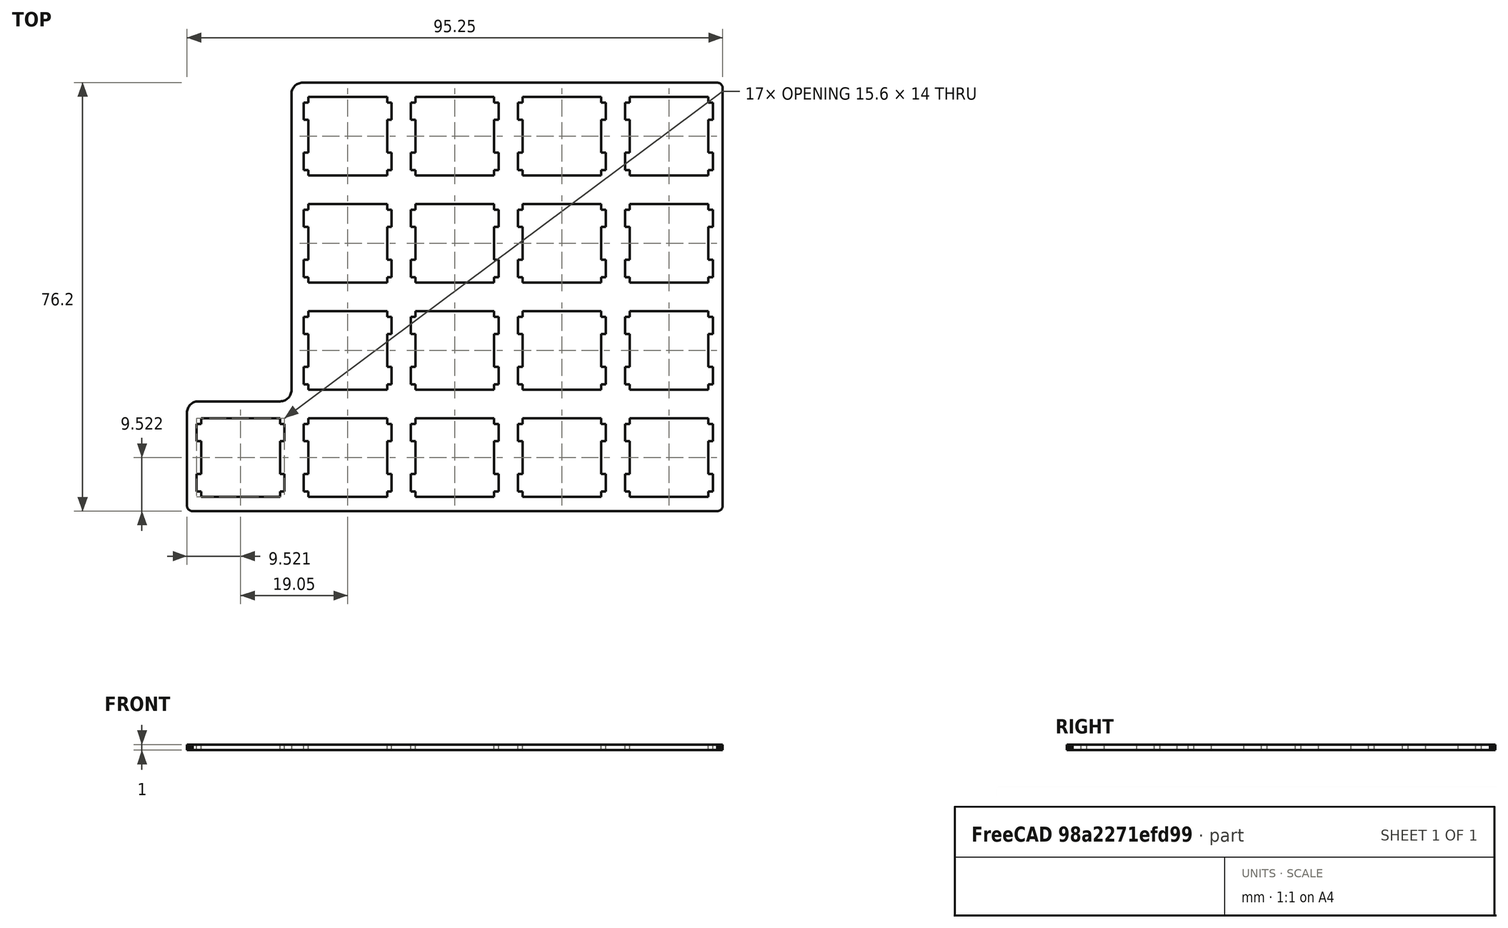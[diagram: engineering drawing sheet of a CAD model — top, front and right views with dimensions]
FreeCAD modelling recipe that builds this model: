
FCSTD DOCUMENT  (FreeCAD 0.20R)
Label: dpad-plate
License: All rights reserved
LicenseURL: http://en.wikipedia.org/wiki/All_rights_reserved
objects: Sketcher::SketchObject×2, PartDesign::Pad×1, PartDesign::Pocket×1, PartDesign::Fillet×1, PartDesign::Body×1
note: 9 computed .brp shape members not serialized (recipe doc carries the construction recipe); baked Part::Feature solids carry a one-line shape summary decoded from their .brp

FEATURE [Sketcher::SketchObject] Sketch
  FullyConstrained = false
  Placement = pos=(0,0,0) rot=(0,0,1;3.14159rad)
  sketch-geometry (424):
    g0: LineSegment StartX=-94.3462 StartY=-76.4575 StartZ=0 EndX=-94.4245 EndY=-76.4551 EndZ=0
    g1: LineSegment StartX=-94.4245 StartY=-76.4551 StartZ=0 EndX=-94.5032 EndY=-76.4452 EndZ=0
    g2: LineSegment StartX=-94.5032 StartY=-76.4452 StartZ=0 EndX=-94.579 EndY=-76.43 EndZ=0
    g3: LineSegment StartX=-94.579 StartY=-76.43 StartZ=0 EndX=-94.6559 EndY=-76.4095 EndZ=0
    g4: LineSegment StartX=-94.6559 StartY=-76.4095 StartZ=0 EndX=-94.729 EndY=-76.382 EndZ=0
    g5: LineSegment StartX=-94.729 StartY=-76.382 StartZ=0 EndX=-94.7995 EndY=-76.3489 EndZ=0
    g6: LineSegment StartX=-94.7995 StartY=-76.3489 StartZ=0 EndX=-94.8683 EndY=-76.3104 EndZ=0
    g7: LineSegment StartX=-94.8683 StartY=-76.3104 StartZ=0 EndX=-94.9332 EndY=-76.2674 EndZ=0
    g8: LineSegment StartX=-94.9332 StartY=-76.2674 StartZ=0 EndX=-94.9949 EndY=-76.218 EndZ=0
    g9: LineSegment StartX=-94.9949 StartY=-76.218 StartZ=0 EndX=-95.0528 EndY=-76.1654 EndZ=0
    g10: LineSegment StartX=-95.0528 StartY=-76.1654 StartZ=0 EndX=-95.1068 EndY=-76.1076 EndZ=0
    g11: LineSegment StartX=-95.1068 StartY=-76.1076 StartZ=0 EndX=-95.1548 EndY=-76.0458 EndZ=0
    g12: LineSegment StartX=-95.1548 StartY=-76.0458 StartZ=0 EndX=-95.1989 EndY=-75.9809 EndZ=0
    g13: LineSegment StartX=-95.1989 StartY=-75.9809 StartZ=0 EndX=-95.2377 EndY=-75.9107 EndZ=0
    g14: LineSegment StartX=-95.2377 StartY=-75.9107 StartZ=0 EndX=-95.2694 EndY=-75.8402 EndZ=0
    g15: LineSegment StartX=-95.2694 StartY=-75.8402 StartZ=0 EndX=-95.2969 EndY=-75.7671 EndZ=0
    g16: LineSegment StartX=-95.2969 StartY=-75.7671 StartZ=0 EndX=-95.3188 EndY=-75.6916 EndZ=0
    g17: LineSegment StartX=-95.3188 StartY=-75.6916 StartZ=0 EndX=-95.334 EndY=-75.6144 EndZ=0
    g18: LineSegment StartX=-95.334 StartY=-75.6144 StartZ=0 EndX=-95.3424 EndY=-75.5357 EndZ=0
    g19: LineSegment StartX=-95.3424 StartY=-75.5357 StartZ=0 EndX=-95.3463 EndY=-75.4574 EndZ=0
    g20: LineSegment StartX=-95.3463 StartY=-75.4574 StartZ=0 EndX=-95.3452 EndY=-1.25677 EndZ=0
    g21: LineSegment StartX=-95.3452 StartY=-1.25677 StartZ=0 EndX=-95.3424 EndY=-1.17822 EndZ=0
    g22: LineSegment StartX=-95.3424 StartY=-1.17822 StartZ=0 EndX=-95.334 EndY=-1.09968 EndZ=0
    g23: LineSegment StartX=-95.334 StartY=-1.09968 StartZ=0 EndX=-95.3188 EndY=-1.02388 EndZ=0
    g24: LineSegment StartX=-95.3188 StartY=-1.02388 StartZ=0 EndX=-95.2969 EndY=-0.946711 EndZ=0
    g25: LineSegment StartX=-95.2969 StartY=-0.946711 StartZ=0 EndX=-95.2694 EndY=-0.873675 EndZ=0
    g26: LineSegment StartX=-95.2694 StartY=-0.873675 StartZ=0 EndX=-95.2377 EndY=-0.803395 EndZ=0
    g27: LineSegment StartX=-95.2377 StartY=-0.803395 StartZ=0 EndX=-95.1989 EndY=-0.734494 EndZ=0
    g28: LineSegment StartX=-95.1989 StartY=-0.734494 StartZ=0 EndX=-95.1548 EndY=-0.669727 EndZ=0
    g29: LineSegment StartX=-95.1548 StartY=-0.669727 StartZ=0 EndX=-95.1068 EndY=-0.607716 EndZ=0
    g30: LineSegment StartX=-95.1068 StartY=-0.607716 StartZ=0 EndX=-95.0528 EndY=-0.549836 EndZ=0
    g31: LineSegment StartX=-95.0528 StartY=-0.549836 StartZ=0 EndX=-94.9949 EndY=-0.496094 EndZ=0
    g32: LineSegment StartX=-94.9949 StartY=-0.496094 StartZ=0 EndX=-94.9332 EndY=-0.447862 EndZ=0
    g33: LineSegment StartX=-94.9332 StartY=-0.447862 StartZ=0 EndX=-94.8683 EndY=-0.403765 EndZ=0
    g34: LineSegment StartX=-94.8683 StartY=-0.403765 StartZ=0 EndX=-94.7995 EndY=-0.365181 EndZ=0
    g35: LineSegment StartX=-94.7995 StartY=-0.365181 StartZ=0 EndX=-94.729 EndY=-0.333485 EndZ=0
    g36: LineSegment StartX=-94.729 StartY=-0.333485 StartZ=0 EndX=-94.6559 EndY=-0.305925 EndZ=0
    g37: LineSegment StartX=-94.6559 StartY=-0.305925 StartZ=0 EndX=-94.579 EndY=-0.283876 EndZ=0
    g38: LineSegment StartX=-94.579 StartY=-0.283876 StartZ=0 EndX=-94.5032 EndY=-0.268718 EndZ=0
    g39: LineSegment StartX=-94.5032 StartY=-0.268718 StartZ=0 EndX=-94.4245 EndY=-0.260449 EndZ=0
    g40: LineSegment StartX=-94.4245 StartY=-0.260449 StartZ=0 EndX=-94.3462 EndY=-0.256315 EndZ=0
    g41: LineSegment StartX=-94.3462 StartY=-0.256315 StartZ=0 EndX=-1.09554 EndY=-0.256315 EndZ=0
    g42: LineSegment StartX=-1.09554 StartY=-0.256315 StartZ=0 EndX=-1.01699 EndY=-0.260449 EndZ=0
    g43: LineSegment StartX=-1.01699 StartY=-0.260449 StartZ=0 EndX=-0.938445 EndY=-0.268718 EndZ=0
    g44: LineSegment StartX=-0.938445 StartY=-0.268718 StartZ=0 EndX=-0.861275 EndY=-0.283876 EndZ=0
    g45: LineSegment StartX=-0.861275 StartY=-0.283876 StartZ=0 EndX=-0.785481 EndY=-0.305925 EndZ=0
    g46: LineSegment StartX=-0.785481 StartY=-0.305925 StartZ=0 EndX=-0.712445 EndY=-0.333485 EndZ=0
    g47: LineSegment StartX=-0.712445 StartY=-0.333485 StartZ=0 EndX=-0.642165 EndY=-0.365181 EndZ=0
    g48: LineSegment StartX=-0.642165 StartY=-0.365181 StartZ=0 EndX=-0.571885 EndY=-0.403765 EndZ=0
    g49: LineSegment StartX=-0.571885 StartY=-0.403765 StartZ=0 EndX=-0.507118 EndY=-0.447862 EndZ=0
    g50: LineSegment StartX=-0.507118 StartY=-0.447862 StartZ=0 EndX=-0.445107 EndY=-0.496094 EndZ=0
    g51: LineSegment StartX=-0.445107 StartY=-0.496094 StartZ=0 EndX=-0.38723 EndY=-0.549836 EndZ=0
    g52: LineSegment StartX=-0.38723 StartY=-0.549836 StartZ=0 EndX=-0.334863 EndY=-0.607716 EndZ=0
    g53: LineSegment StartX=-0.334863 StartY=-0.607716 StartZ=0 EndX=-0.285254 EndY=-0.669727 EndZ=0
    g54: LineSegment StartX=-0.285254 StartY=-0.669727 StartZ=0 EndX=-0.242535 EndY=-0.734494 EndZ=0
    g55: LineSegment StartX=-0.242535 StartY=-0.734494 StartZ=0 EndX=-0.20395 EndY=-0.803395 EndZ=0
    g56: LineSegment StartX=-0.20395 StartY=-0.803395 StartZ=0 EndX=-0.170877 EndY=-0.873675 EndZ=0
    g57: LineSegment StartX=-0.170877 StartY=-0.873675 StartZ=0 EndX=-0.143316 EndY=-0.946711 EndZ=0
    g58: LineSegment StartX=-0.143316 StartY=-0.946711 StartZ=0 EndX=-0.122645 EndY=-1.02388 EndZ=0
    g59: LineSegment StartX=-0.122645 StartY=-1.02388 StartZ=0 EndX=-0.107487 EndY=-1.09968 EndZ=0
    g60: LineSegment StartX=-0.107487 StartY=-1.09968 StartZ=0 EndX=-0.0978408 EndY=-1.17822 EndZ=0
    g61: LineSegment StartX=-0.0978408 StartY=-1.17822 StartZ=0 EndX=-0.0950846 EndY=-1.25677 EndZ=0
    g62: LineSegment StartX=-0.0950846 StartY=-1.25677 StartZ=0 EndX=-0.0950846 EndY=-75.4574 EndZ=0
    g63: LineSegment StartX=-0.0950846 StartY=-75.4574 StartZ=0 EndX=-0.0978408 EndY=-75.5357 EndZ=0
    g64: LineSegment StartX=-0.0978408 StartY=-75.5357 StartZ=0 EndX=-0.107487 EndY=-75.6144 EndZ=0
    g65: LineSegment StartX=-0.107487 StartY=-75.6144 StartZ=0 EndX=-0.122645 EndY=-75.6916 EndZ=0
    g66: LineSegment StartX=-0.122645 StartY=-75.6916 StartZ=0 EndX=-0.143316 EndY=-75.7671 EndZ=0
    g67: LineSegment StartX=-0.143316 StartY=-75.7671 StartZ=0 EndX=-0.170877 EndY=-75.8402 EndZ=0
    g68: LineSegment StartX=-0.170877 StartY=-75.8402 StartZ=0 EndX=-0.20395 EndY=-75.9107 EndZ=0
    g69: LineSegment StartX=-0.20395 StartY=-75.9107 StartZ=0 EndX=-0.242535 EndY=-75.9809 EndZ=0
    g70: LineSegment StartX=-0.242535 StartY=-75.9809 StartZ=0 EndX=-0.285254 EndY=-76.0458 EndZ=0
    g71: LineSegment StartX=-0.285254 StartY=-76.0458 StartZ=0 EndX=-0.334863 EndY=-76.1076 EndZ=0
    g72: LineSegment StartX=-0.334863 StartY=-76.1076 StartZ=0 EndX=-0.38723 EndY=-76.1654 EndZ=0
    g73: LineSegment StartX=-0.38723 StartY=-76.1654 StartZ=0 EndX=-0.445107 EndY=-76.218 EndZ=0
    g74: LineSegment StartX=-0.445107 StartY=-76.218 StartZ=0 EndX=-0.507118 EndY=-76.2674 EndZ=0
    g75: LineSegment StartX=-0.507118 StartY=-76.2674 StartZ=0 EndX=-0.571885 EndY=-76.3104 EndZ=0
    g76: LineSegment StartX=-0.571885 StartY=-76.3104 StartZ=0 EndX=-0.642165 EndY=-76.3489 EndZ=0
    g77: LineSegment StartX=-0.642165 StartY=-76.3489 StartZ=0 EndX=-0.712445 EndY=-76.382 EndZ=0
    g78: LineSegment StartX=-0.712445 StartY=-76.382 StartZ=0 EndX=-0.785481 EndY=-76.4095 EndZ=0
    g79: LineSegment StartX=-0.785481 StartY=-76.4095 StartZ=0 EndX=-0.861275 EndY=-76.43 EndZ=0
    g80: LineSegment StartX=-0.861275 StartY=-76.43 StartZ=0 EndX=-0.938445 EndY=-76.4452 EndZ=0
    g81: LineSegment StartX=-0.938445 StartY=-76.4452 StartZ=0 EndX=-1.01699 EndY=-76.4551 EndZ=0
    g82: LineSegment StartX=-1.01699 StartY=-76.4551 StartZ=0 EndX=-1.09554 EndY=-76.4575 EndZ=0
    g83: LineSegment StartX=-1.09554 StartY=-76.4575 StartZ=0 EndX=-94.3462 EndY=-76.4575 EndZ=0
    g84: LineSegment StartX=-2.62103 StartY=-16.7817 StartZ=0 EndX=-2.62103 EndY=-15.7827 EndZ=0
    g85: LineSegment StartX=-2.62103 StartY=-15.7827 StartZ=0 EndX=-1.82039 EndY=-15.7827 EndZ=0
    g86: LineSegment StartX=-1.82039 StartY=-15.7827 StartZ=0 EndX=-1.82039 EndY=-12.6835 EndZ=0
    g87: LineSegment StartX=-1.82039 StartY=-12.6835 StartZ=0 EndX=-2.62103 EndY=-12.6835 EndZ=0
    g88: LineSegment StartX=-2.62103 StartY=-12.6835 StartZ=0 EndX=-2.62103 EndY=-6.88192 EndZ=0
    g89: LineSegment StartX=-2.62103 StartY=-6.88192 StartZ=0 EndX=-1.82039 EndY=-6.88192 EndZ=0
    g90: LineSegment StartX=-1.82039 StartY=-6.88192 StartZ=0 EndX=-1.82039 EndY=-3.78273 EndZ=0
    g91: LineSegment StartX=-1.82039 StartY=-3.78273 StartZ=0 EndX=-2.62103 EndY=-3.78273 EndZ=0
    g92: LineSegment StartX=-2.62103 StartY=-3.78273 StartZ=0 EndX=-2.62103 EndY=-2.78226 EndZ=0
    g93: LineSegment StartX=-2.62103 StartY=-2.78226 StartZ=0 EndX=-16.6205 EndY=-2.78226 EndZ=0
    g94: LineSegment StartX=-16.6205 StartY=-2.78226 StartZ=0 EndX=-16.6205 EndY=-3.78273 EndZ=0
    g95: LineSegment StartX=-16.6205 StartY=-3.78273 StartZ=0 EndX=-17.4212 EndY=-3.78273 EndZ=0
    g96: LineSegment StartX=-17.4212 StartY=-3.78273 StartZ=0 EndX=-17.4212 EndY=-6.88192 EndZ=0
    g97: LineSegment StartX=-17.4212 StartY=-6.88192 StartZ=0 EndX=-16.6205 EndY=-6.88192 EndZ=0
    g98: LineSegment StartX=-16.6205 StartY=-6.88192 StartZ=0 EndX=-16.6205 EndY=-12.6835 EndZ=0
    g99: LineSegment StartX=-16.6205 StartY=-12.6835 StartZ=0 EndX=-17.4212 EndY=-12.6835 EndZ=0
    g100: LineSegment StartX=-17.4212 StartY=-12.6835 StartZ=0 EndX=-17.4212 EndY=-15.7827 EndZ=0
    g101: LineSegment StartX=-17.4212 StartY=-15.7827 StartZ=0 EndX=-16.6205 EndY=-15.7827 EndZ=0
    g102: LineSegment StartX=-16.6205 StartY=-15.7827 StartZ=0 EndX=-16.6205 EndY=-16.7817 EndZ=0
    g103: LineSegment StartX=-16.6205 StartY=-16.7817 StartZ=0 EndX=-2.62103 EndY=-16.7817 EndZ=0
    g104: LineSegment StartX=-21.671 StartY=-16.7817 StartZ=0 EndX=-21.671 EndY=-15.7827 EndZ=0
    g105: LineSegment StartX=-21.671 StartY=-15.7827 StartZ=0 EndX=-20.8704 EndY=-15.7827 EndZ=0
    g106: LineSegment StartX=-20.8704 StartY=-15.7827 StartZ=0 EndX=-20.8704 EndY=-12.6835 EndZ=0
    g107: LineSegment StartX=-20.8704 StartY=-12.6835 StartZ=0 EndX=-21.671 EndY=-12.6835 EndZ=0
    g108: LineSegment StartX=-21.671 StartY=-12.6835 StartZ=0 EndX=-21.671 EndY=-6.88192 EndZ=0
    g109: LineSegment StartX=-21.671 StartY=-6.88192 StartZ=0 EndX=-20.8704 EndY=-6.88192 EndZ=0
    g110: LineSegment StartX=-20.8704 StartY=-6.88192 StartZ=0 EndX=-20.8704 EndY=-3.78273 EndZ=0
    g111: LineSegment StartX=-20.8704 StartY=-3.78273 StartZ=0 EndX=-21.671 EndY=-3.78273 EndZ=0
    g112: LineSegment StartX=-21.671 StartY=-3.78273 StartZ=0 EndX=-21.671 EndY=-2.78226 EndZ=0
    g113: LineSegment StartX=-21.671 StartY=-2.78226 StartZ=0 EndX=-35.6704 EndY=-2.78226 EndZ=0
    g114: LineSegment StartX=-35.6704 StartY=-2.78226 StartZ=0 EndX=-35.6704 EndY=-3.78273 EndZ=0
    g115: LineSegment StartX=-35.6704 StartY=-3.78273 StartZ=0 EndX=-36.4712 EndY=-3.78273 EndZ=0
    g116: LineSegment StartX=-36.4712 StartY=-3.78273 StartZ=0 EndX=-36.4712 EndY=-6.88192 EndZ=0
    g117: LineSegment StartX=-36.4712 StartY=-6.88192 StartZ=0 EndX=-35.6704 EndY=-6.88192 EndZ=0
    g118: LineSegment StartX=-35.6704 StartY=-6.88192 StartZ=0 EndX=-35.6704 EndY=-12.6835 EndZ=0
    g119: LineSegment StartX=-35.6704 StartY=-12.6835 StartZ=0 EndX=-36.4712 EndY=-12.6835 EndZ=0
    g120: LineSegment StartX=-36.4712 StartY=-12.6835 StartZ=0 EndX=-36.4712 EndY=-15.7827 EndZ=0
    g121: LineSegment StartX=-36.4712 StartY=-15.7827 StartZ=0 EndX=-35.6704 EndY=-15.7827 EndZ=0
    g122: LineSegment StartX=-35.6704 StartY=-15.7827 StartZ=0 EndX=-35.6704 EndY=-16.7817 EndZ=0
    g123: LineSegment StartX=-35.6704 StartY=-16.7817 StartZ=0 EndX=-21.671 EndY=-16.7817 EndZ=0
    g124: LineSegment StartX=-40.7211 StartY=-16.7817 StartZ=0 EndX=-40.7211 EndY=-15.7827 EndZ=0
    g125: LineSegment StartX=-40.7211 StartY=-15.7827 StartZ=0 EndX=-39.9203 EndY=-15.7827 EndZ=0
    g126: LineSegment StartX=-39.9203 StartY=-15.7827 StartZ=0 EndX=-39.9203 EndY=-12.6835 EndZ=0
    g127: LineSegment StartX=-39.9203 StartY=-12.6835 StartZ=0 EndX=-40.7211 EndY=-12.6835 EndZ=0
    g128: LineSegment StartX=-40.7211 StartY=-12.6835 StartZ=0 EndX=-40.7211 EndY=-6.88192 EndZ=0
    g129: LineSegment StartX=-40.7211 StartY=-6.88192 StartZ=0 EndX=-39.9203 EndY=-6.88192 EndZ=0
    g130: LineSegment StartX=-39.9203 StartY=-6.88192 StartZ=0 EndX=-39.9203 EndY=-3.78273 EndZ=0
    g131: LineSegment StartX=-39.9203 StartY=-3.78273 StartZ=0 EndX=-40.7211 EndY=-3.78273 EndZ=0
    g132: LineSegment StartX=-40.7211 StartY=-3.78273 StartZ=0 EndX=-40.7211 EndY=-2.78226 EndZ=0
    g133: LineSegment StartX=-40.7211 StartY=-2.78226 StartZ=0 EndX=-54.7204 EndY=-2.78226 EndZ=0
    g134: LineSegment StartX=-54.7204 StartY=-2.78226 StartZ=0 EndX=-54.7204 EndY=-3.78273 EndZ=0
    g135: LineSegment StartX=-54.7204 StartY=-3.78273 StartZ=0 EndX=-55.5212 EndY=-3.78273 EndZ=0
    g136: LineSegment StartX=-55.5212 StartY=-3.78273 StartZ=0 EndX=-55.5212 EndY=-6.88192 EndZ=0
    g137: LineSegment StartX=-55.5212 StartY=-6.88192 StartZ=0 EndX=-54.7204 EndY=-6.88192 EndZ=0
    g138: LineSegment StartX=-54.7204 StartY=-6.88192 StartZ=0 EndX=-54.7204 EndY=-12.6835 EndZ=0
    g139: LineSegment StartX=-54.7204 StartY=-12.6835 StartZ=0 EndX=-55.5212 EndY=-12.6835 EndZ=0
    g140: LineSegment StartX=-55.5212 StartY=-12.6835 StartZ=0 EndX=-55.5212 EndY=-15.7827 EndZ=0
    g141: LineSegment StartX=-55.5212 StartY=-15.7827 StartZ=0 EndX=-54.7204 EndY=-15.7827 EndZ=0
    g142: LineSegment StartX=-54.7204 StartY=-15.7827 StartZ=0 EndX=-54.7204 EndY=-16.7817 EndZ=0
    g143: LineSegment StartX=-54.7204 StartY=-16.7817 StartZ=0 EndX=-40.7211 EndY=-16.7817 EndZ=0
    g144: LineSegment StartX=-59.7711 StartY=-16.7817 StartZ=0 EndX=-59.7711 EndY=-15.7827 EndZ=0
    g145: LineSegment StartX=-59.7711 StartY=-15.7827 StartZ=0 EndX=-58.9703 EndY=-15.7827 EndZ=0
    g146: LineSegment StartX=-58.9703 StartY=-15.7827 StartZ=0 EndX=-58.9703 EndY=-12.6835 EndZ=0
    g147: LineSegment StartX=-58.9703 StartY=-12.6835 StartZ=0 EndX=-59.7711 EndY=-12.6835 EndZ=0
    g148: LineSegment StartX=-59.7711 StartY=-12.6835 StartZ=0 EndX=-59.7711 EndY=-6.88192 EndZ=0
    g149: LineSegment StartX=-59.7711 StartY=-6.88192 StartZ=0 EndX=-58.9703 EndY=-6.88192 EndZ=0
    g150: LineSegment StartX=-58.9703 StartY=-6.88192 StartZ=0 EndX=-58.9703 EndY=-3.78273 EndZ=0
    g151: LineSegment StartX=-58.9703 StartY=-3.78273 StartZ=0 EndX=-59.7711 EndY=-3.78273 EndZ=0
    g152: LineSegment StartX=-59.7711 StartY=-3.78273 StartZ=0 EndX=-59.7711 EndY=-2.78226 EndZ=0
    g153: LineSegment StartX=-59.7711 StartY=-2.78226 StartZ=0 EndX=-73.7704 EndY=-2.78226 EndZ=0
    g154: LineSegment StartX=-73.7704 StartY=-2.78226 StartZ=0 EndX=-73.7704 EndY=-3.78273 EndZ=0
    g155: LineSegment StartX=-73.7704 StartY=-3.78273 StartZ=0 EndX=-74.5712 EndY=-3.78273 EndZ=0
    g156: LineSegment StartX=-74.5712 StartY=-3.78273 StartZ=0 EndX=-74.5712 EndY=-6.88192 EndZ=0
    g157: LineSegment StartX=-74.5712 StartY=-6.88192 StartZ=0 EndX=-73.7704 EndY=-6.88192 EndZ=0
    g158: LineSegment StartX=-73.7704 StartY=-6.88192 StartZ=0 EndX=-73.7704 EndY=-12.6835 EndZ=0
    g159: LineSegment StartX=-73.7704 StartY=-12.6835 StartZ=0 EndX=-74.5712 EndY=-12.6835 EndZ=0
    g160: LineSegment StartX=-74.5712 StartY=-12.6835 StartZ=0 EndX=-74.5712 EndY=-15.7827 EndZ=0
    g161: LineSegment StartX=-74.5712 StartY=-15.7827 StartZ=0 EndX=-73.7704 EndY=-15.7827 EndZ=0
    g162: LineSegment StartX=-73.7704 StartY=-15.7827 StartZ=0 EndX=-73.7704 EndY=-16.7817 EndZ=0
    g163: LineSegment StartX=-73.7704 StartY=-16.7817 StartZ=0 EndX=-59.7711 EndY=-16.7817 EndZ=0
    g164: LineSegment StartX=-78.8211 StartY=-16.7817 StartZ=0 EndX=-78.8211 EndY=-15.7827 EndZ=0
    g165: LineSegment StartX=-78.8211 StartY=-15.7827 StartZ=0 EndX=-78.0203 EndY=-15.7827 EndZ=0
    g166: LineSegment StartX=-78.0203 StartY=-15.7827 StartZ=0 EndX=-78.0203 EndY=-12.6835 EndZ=0
    g167: LineSegment StartX=-78.0203 StartY=-12.6835 StartZ=0 EndX=-78.8211 EndY=-12.6835 EndZ=0
    g168: LineSegment StartX=-78.8211 StartY=-12.6835 StartZ=0 EndX=-78.8211 EndY=-6.88192 EndZ=0
    g169: LineSegment StartX=-78.8211 StartY=-6.88192 StartZ=0 EndX=-78.0203 EndY=-6.88192 EndZ=0
    g170: LineSegment StartX=-78.0203 StartY=-6.88192 StartZ=0 EndX=-78.0203 EndY=-3.78273 EndZ=0
    g171: LineSegment StartX=-78.0203 StartY=-3.78273 StartZ=0 EndX=-78.8211 EndY=-3.78273 EndZ=0
    g172: LineSegment StartX=-78.8211 StartY=-3.78273 StartZ=0 EndX=-78.8211 EndY=-2.78226 EndZ=0
    g173: LineSegment StartX=-78.8211 StartY=-2.78226 StartZ=0 EndX=-92.8204 EndY=-2.78226 EndZ=0
    g174: LineSegment StartX=-92.8204 StartY=-2.78226 StartZ=0 EndX=-92.8204 EndY=-3.78273 EndZ=0
    g175: LineSegment StartX=-92.8204 StartY=-3.78273 StartZ=0 EndX=-93.6198 EndY=-3.78273 EndZ=0
    g176: LineSegment StartX=-93.6198 StartY=-3.78273 StartZ=0 EndX=-93.6198 EndY=-6.88192 EndZ=0
    g177: LineSegment StartX=-93.6198 StartY=-6.88192 StartZ=0 EndX=-92.8204 EndY=-6.88192 EndZ=0
    g178: LineSegment StartX=-92.8204 StartY=-6.88192 StartZ=0 EndX=-92.8204 EndY=-12.6835 EndZ=0
    g179: LineSegment StartX=-92.8204 StartY=-12.6835 StartZ=0 EndX=-93.6198 EndY=-12.6835 EndZ=0
    g180: LineSegment StartX=-93.6198 StartY=-12.6835 StartZ=0 EndX=-93.6198 EndY=-15.7827 EndZ=0
    g181: LineSegment StartX=-93.6198 StartY=-15.7827 StartZ=0 EndX=-92.8204 EndY=-15.7827 EndZ=0
    g182: LineSegment StartX=-92.8204 StartY=-15.7827 StartZ=0 EndX=-92.8204 EndY=-16.7817 EndZ=0
    g183: LineSegment StartX=-92.8204 StartY=-16.7817 StartZ=0 EndX=-78.8211 EndY=-16.7817 EndZ=0
    g184: LineSegment StartX=-21.671 StartY=-35.8316 StartZ=0 EndX=-21.671 EndY=-34.8327 EndZ=0
    g185: LineSegment StartX=-21.671 StartY=-34.8327 StartZ=0 EndX=-20.8704 EndY=-34.8327 EndZ=0
    g186: LineSegment StartX=-20.8704 StartY=-34.8327 StartZ=0 EndX=-20.8704 EndY=-31.7321 EndZ=0
    g187: LineSegment StartX=-20.8704 StartY=-31.7321 StartZ=0 EndX=-21.671 EndY=-31.7321 EndZ=0
    g188: LineSegment StartX=-21.671 StartY=-31.7321 StartZ=0 EndX=-21.671 EndY=-25.9319 EndZ=0
    g189: LineSegment StartX=-21.671 StartY=-25.9319 StartZ=0 EndX=-20.8704 EndY=-25.9319 EndZ=0
    g190: LineSegment StartX=-20.8704 StartY=-25.9319 StartZ=0 EndX=-20.8704 EndY=-22.8327 EndZ=0
    g191: LineSegment StartX=-20.8704 StartY=-22.8327 StartZ=0 EndX=-21.671 EndY=-22.8327 EndZ=0
    g192: LineSegment StartX=-21.671 StartY=-22.8327 StartZ=0 EndX=-21.671 EndY=-21.8323 EndZ=0
    g193: LineSegment StartX=-21.671 StartY=-21.8323 StartZ=0 EndX=-35.6704 EndY=-21.8323 EndZ=0
    g194: LineSegment StartX=-35.6704 StartY=-21.8323 StartZ=0 EndX=-35.6704 EndY=-22.8327 EndZ=0
    g195: LineSegment StartX=-35.6704 StartY=-22.8327 StartZ=0 EndX=-36.4712 EndY=-22.8327 EndZ=0
    g196: LineSegment StartX=-36.4712 StartY=-22.8327 StartZ=0 EndX=-36.4712 EndY=-25.9319 EndZ=0
    g197: LineSegment StartX=-36.4712 StartY=-25.9319 StartZ=0 EndX=-35.6704 EndY=-25.9319 EndZ=0
    g198: LineSegment StartX=-35.6704 StartY=-25.9319 StartZ=0 EndX=-35.6704 EndY=-31.7321 EndZ=0
    g199: LineSegment StartX=-35.6704 StartY=-31.7321 StartZ=0 EndX=-36.4712 EndY=-31.7321 EndZ=0
    g200: LineSegment StartX=-36.4712 StartY=-31.7321 StartZ=0 EndX=-36.4712 EndY=-34.8327 EndZ=0
    g201: LineSegment StartX=-36.4712 StartY=-34.8327 StartZ=0 EndX=-35.6704 EndY=-34.8327 EndZ=0
    g202: LineSegment StartX=-35.6704 StartY=-34.8327 StartZ=0 EndX=-35.6704 EndY=-35.8316 EndZ=0
    g203: LineSegment StartX=-35.6704 StartY=-35.8316 StartZ=0 EndX=-21.671 EndY=-35.8316 EndZ=0
    g204: LineSegment StartX=-40.7211 StartY=-35.8316 StartZ=0 EndX=-40.7211 EndY=-34.8327 EndZ=0
    g205: LineSegment StartX=-40.7211 StartY=-34.8327 StartZ=0 EndX=-39.9203 EndY=-34.8327 EndZ=0
    g206: LineSegment StartX=-39.9203 StartY=-34.8327 StartZ=0 EndX=-39.9203 EndY=-31.7321 EndZ=0
    g207: LineSegment StartX=-39.9203 StartY=-31.7321 StartZ=0 EndX=-40.7211 EndY=-31.7321 EndZ=0
    g208: LineSegment StartX=-40.7211 StartY=-31.7321 StartZ=0 EndX=-40.7211 EndY=-25.9319 EndZ=0
    g209: LineSegment StartX=-40.7211 StartY=-25.9319 StartZ=0 EndX=-39.9203 EndY=-25.9319 EndZ=0
    g210: LineSegment StartX=-39.9203 StartY=-25.9319 StartZ=0 EndX=-39.9203 EndY=-22.8327 EndZ=0
    g211: LineSegment StartX=-39.9203 StartY=-22.8327 StartZ=0 EndX=-40.7211 EndY=-22.8327 EndZ=0
    g212: LineSegment StartX=-40.7211 StartY=-22.8327 StartZ=0 EndX=-40.7211 EndY=-21.8323 EndZ=0
    g213: LineSegment StartX=-40.7211 StartY=-21.8323 StartZ=0 EndX=-54.7204 EndY=-21.8323 EndZ=0
    g214: LineSegment StartX=-54.7204 StartY=-21.8323 StartZ=0 EndX=-54.7204 EndY=-22.8327 EndZ=0
    g215: LineSegment StartX=-54.7204 StartY=-22.8327 StartZ=0 EndX=-55.5212 EndY=-22.8327 EndZ=0
    g216: LineSegment StartX=-55.5212 StartY=-22.8327 StartZ=0 EndX=-55.5212 EndY=-25.9319 EndZ=0
    g217: LineSegment StartX=-55.5212 StartY=-25.9319 StartZ=0 EndX=-54.7204 EndY=-25.9319 EndZ=0
    g218: LineSegment StartX=-54.7204 StartY=-25.9319 StartZ=0 EndX=-54.7204 EndY=-31.7321 EndZ=0
    g219: LineSegment StartX=-54.7204 StartY=-31.7321 StartZ=0 EndX=-55.5212 EndY=-31.7321 EndZ=0
    g220: LineSegment StartX=-55.5212 StartY=-31.7321 StartZ=0 EndX=-55.5212 EndY=-34.8327 EndZ=0
    g221: LineSegment StartX=-55.5212 StartY=-34.8327 StartZ=0 EndX=-54.7204 EndY=-34.8327 EndZ=0
    g222: LineSegment StartX=-54.7204 StartY=-34.8327 StartZ=0 EndX=-54.7204 EndY=-35.8316 EndZ=0
    g223: LineSegment StartX=-54.7204 StartY=-35.8316 StartZ=0 EndX=-40.7211 EndY=-35.8316 EndZ=0
    g224: LineSegment StartX=-59.7711 StartY=-35.8316 StartZ=0 EndX=-59.7711 EndY=-34.8327 EndZ=0
    g225: LineSegment StartX=-59.7711 StartY=-34.8327 StartZ=0 EndX=-58.9703 EndY=-34.8327 EndZ=0
    g226: LineSegment StartX=-58.9703 StartY=-34.8327 StartZ=0 EndX=-58.9703 EndY=-31.7321 EndZ=0
    g227: LineSegment StartX=-58.9703 StartY=-31.7321 StartZ=0 EndX=-59.7711 EndY=-31.7321 EndZ=0
    g228: LineSegment StartX=-59.7711 StartY=-31.7321 StartZ=0 EndX=-59.7711 EndY=-25.9319 EndZ=0
    g229: LineSegment StartX=-59.7711 StartY=-25.9319 StartZ=0 EndX=-58.9703 EndY=-25.9319 EndZ=0
    g230: LineSegment StartX=-58.9703 StartY=-25.9319 StartZ=0 EndX=-58.9703 EndY=-22.8327 EndZ=0
    g231: LineSegment StartX=-58.9703 StartY=-22.8327 StartZ=0 EndX=-59.7711 EndY=-22.8327 EndZ=0
    g232: LineSegment StartX=-59.7711 StartY=-22.8327 StartZ=0 EndX=-59.7711 EndY=-21.8323 EndZ=0
    g233: LineSegment StartX=-59.7711 StartY=-21.8323 StartZ=0 EndX=-73.7704 EndY=-21.8323 EndZ=0
    g234: LineSegment StartX=-73.7704 StartY=-21.8323 StartZ=0 EndX=-73.7704 EndY=-22.8327 EndZ=0
    g235: LineSegment StartX=-73.7704 StartY=-22.8327 StartZ=0 EndX=-74.5712 EndY=-22.8327 EndZ=0
    g236: LineSegment StartX=-74.5712 StartY=-22.8327 StartZ=0 EndX=-74.5712 EndY=-25.9319 EndZ=0
    g237: LineSegment StartX=-74.5712 StartY=-25.9319 StartZ=0 EndX=-73.7704 EndY=-25.9319 EndZ=0
    g238: LineSegment StartX=-73.7704 StartY=-25.9319 StartZ=0 EndX=-73.7704 EndY=-31.7321 EndZ=0
    g239: LineSegment StartX=-73.7704 StartY=-31.7321 StartZ=0 EndX=-74.5712 EndY=-31.7321 EndZ=0
    g240: LineSegment StartX=-74.5712 StartY=-31.7321 StartZ=0 EndX=-74.5712 EndY=-34.8327 EndZ=0
    g241: LineSegment StartX=-74.5712 StartY=-34.8327 StartZ=0 EndX=-73.7704 EndY=-34.8327 EndZ=0
    g242: LineSegment StartX=-73.7704 StartY=-34.8327 StartZ=0 EndX=-73.7704 EndY=-35.8316 EndZ=0
    g243: LineSegment StartX=-73.7704 StartY=-35.8316 StartZ=0 EndX=-59.7711 EndY=-35.8316 EndZ=0
    g244: LineSegment StartX=-78.8211 StartY=-35.8316 StartZ=0 EndX=-78.8211 EndY=-34.8327 EndZ=0
    g245: LineSegment StartX=-78.8211 StartY=-34.8327 StartZ=0 EndX=-78.0203 EndY=-34.8327 EndZ=0
    g246: LineSegment StartX=-78.0203 StartY=-34.8327 StartZ=0 EndX=-78.0203 EndY=-31.7321 EndZ=0
    g247: LineSegment StartX=-78.0203 StartY=-31.7321 StartZ=0 EndX=-78.8211 EndY=-31.7321 EndZ=0
    g248: LineSegment StartX=-78.8211 StartY=-31.7321 StartZ=0 EndX=-78.8211 EndY=-25.9319 EndZ=0
    g249: LineSegment StartX=-78.8211 StartY=-25.9319 StartZ=0 EndX=-78.0203 EndY=-25.9319 EndZ=0
    g250: LineSegment StartX=-78.0203 StartY=-25.9319 StartZ=0 EndX=-78.0203 EndY=-22.8327 EndZ=0
    g251: LineSegment StartX=-78.0203 StartY=-22.8327 StartZ=0 EndX=-78.8211 EndY=-22.8327 EndZ=0
    g252: LineSegment StartX=-78.8211 StartY=-22.8327 StartZ=0 EndX=-78.8211 EndY=-21.8323 EndZ=0
    g253: LineSegment StartX=-78.8211 StartY=-21.8323 StartZ=0 EndX=-92.8204 EndY=-21.8323 EndZ=0
    g254: LineSegment StartX=-92.8204 StartY=-21.8323 StartZ=0 EndX=-92.8204 EndY=-22.8327 EndZ=0
    g255: LineSegment StartX=-92.8204 StartY=-22.8327 StartZ=0 EndX=-93.6198 EndY=-22.8327 EndZ=0
    g256: LineSegment StartX=-93.6198 StartY=-22.8327 StartZ=0 EndX=-93.6198 EndY=-25.9319 EndZ=0
    g257: LineSegment StartX=-93.6198 StartY=-25.9319 StartZ=0 EndX=-92.8204 EndY=-25.9319 EndZ=0
    g258: LineSegment StartX=-92.8204 StartY=-25.9319 StartZ=0 EndX=-92.8204 EndY=-31.7321 EndZ=0
    g259: LineSegment StartX=-92.8204 StartY=-31.7321 StartZ=0 EndX=-93.6198 EndY=-31.7321 EndZ=0
    g260: LineSegment StartX=-93.6198 StartY=-31.7321 StartZ=0 EndX=-93.6198 EndY=-34.8327 EndZ=0
    g261: LineSegment StartX=-93.6198 StartY=-34.8327 StartZ=0 EndX=-92.8204 EndY=-34.8327 EndZ=0
    g262: LineSegment StartX=-92.8204 StartY=-34.8327 StartZ=0 EndX=-92.8204 EndY=-35.8316 EndZ=0
    g263: LineSegment StartX=-92.8204 StartY=-35.8316 StartZ=0 EndX=-78.8211 EndY=-35.8316 EndZ=0
    g264: LineSegment StartX=-21.671 StartY=-54.8816 StartZ=0 EndX=-21.671 EndY=-53.8826 EndZ=0
    g265: LineSegment StartX=-21.671 StartY=-53.8826 StartZ=0 EndX=-20.8704 EndY=-53.8826 EndZ=0
    g266: LineSegment StartX=-20.8704 StartY=-53.8826 StartZ=0 EndX=-20.8704 EndY=-50.782 EndZ=0
    g267: LineSegment StartX=-20.8704 StartY=-50.782 StartZ=0 EndX=-21.671 EndY=-50.782 EndZ=0
    g268: LineSegment StartX=-21.671 StartY=-50.782 StartZ=0 EndX=-21.671 EndY=-44.982 EndZ=0
    g269: LineSegment StartX=-21.671 StartY=-44.982 StartZ=0 EndX=-20.8704 EndY=-44.982 EndZ=0
    g270: LineSegment StartX=-20.8704 StartY=-44.982 StartZ=0 EndX=-20.8704 EndY=-41.8828 EndZ=0
    g271: LineSegment StartX=-20.8704 StartY=-41.8828 StartZ=0 EndX=-21.671 EndY=-41.8828 EndZ=0
    g272: LineSegment StartX=-21.671 StartY=-41.8828 StartZ=0 EndX=-21.671 EndY=-40.8824 EndZ=0
    g273: LineSegment StartX=-21.671 StartY=-40.8824 StartZ=0 EndX=-35.6704 EndY=-40.8824 EndZ=0
    g274: LineSegment StartX=-35.6704 StartY=-40.8824 StartZ=0 EndX=-35.6704 EndY=-41.8828 EndZ=0
    g275: LineSegment StartX=-35.6704 StartY=-41.8828 StartZ=0 EndX=-36.4712 EndY=-41.8828 EndZ=0
    g276: LineSegment StartX=-36.4712 StartY=-41.8828 StartZ=0 EndX=-36.4712 EndY=-44.982 EndZ=0
    g277: LineSegment StartX=-36.4712 StartY=-44.982 StartZ=0 EndX=-35.6704 EndY=-44.982 EndZ=0
    g278: LineSegment StartX=-35.6704 StartY=-44.982 StartZ=0 EndX=-35.6704 EndY=-50.782 EndZ=0
    g279: LineSegment StartX=-35.6704 StartY=-50.782 StartZ=0 EndX=-36.4712 EndY=-50.782 EndZ=0
    g280: LineSegment StartX=-36.4712 StartY=-50.782 StartZ=0 EndX=-36.4712 EndY=-53.8826 EndZ=0
    g281: LineSegment StartX=-36.4712 StartY=-53.8826 StartZ=0 EndX=-35.6704 EndY=-53.8826 EndZ=0
    g282: LineSegment StartX=-35.6704 StartY=-53.8826 StartZ=0 EndX=-35.6704 EndY=-54.8816 EndZ=0
    g283: LineSegment StartX=-35.6704 StartY=-54.8816 StartZ=0 EndX=-21.671 EndY=-54.8816 EndZ=0
    g284: LineSegment StartX=-40.7211 StartY=-54.8816 StartZ=0 EndX=-40.7211 EndY=-53.8826 EndZ=0
    g285: LineSegment StartX=-40.7211 StartY=-53.8826 StartZ=0 EndX=-39.9203 EndY=-53.8826 EndZ=0
    g286: LineSegment StartX=-39.9203 StartY=-53.8826 StartZ=0 EndX=-39.9203 EndY=-50.782 EndZ=0
    g287: LineSegment StartX=-39.9203 StartY=-50.782 StartZ=0 EndX=-40.7211 EndY=-50.782 EndZ=0
    g288: LineSegment StartX=-40.7211 StartY=-50.782 StartZ=0 EndX=-40.7211 EndY=-44.982 EndZ=0
    g289: LineSegment StartX=-40.7211 StartY=-44.982 StartZ=0 EndX=-39.9203 EndY=-44.982 EndZ=0
    g290: LineSegment StartX=-39.9203 StartY=-44.982 StartZ=0 EndX=-39.9203 EndY=-41.8828 EndZ=0
    g291: LineSegment StartX=-39.9203 StartY=-41.8828 StartZ=0 EndX=-40.7211 EndY=-41.8828 EndZ=0
    g292: LineSegment StartX=-40.7211 StartY=-41.8828 StartZ=0 EndX=-40.7211 EndY=-40.8824 EndZ=0
    g293: LineSegment StartX=-40.7211 StartY=-40.8824 StartZ=0 EndX=-54.7204 EndY=-40.8824 EndZ=0
    g294: LineSegment StartX=-54.7204 StartY=-40.8824 StartZ=0 EndX=-54.7204 EndY=-41.8828 EndZ=0
    g295: LineSegment StartX=-54.7204 StartY=-41.8828 StartZ=0 EndX=-55.5212 EndY=-41.8828 EndZ=0
    g296: LineSegment StartX=-55.5212 StartY=-41.8828 StartZ=0 EndX=-55.5212 EndY=-44.982 EndZ=0
    g297: LineSegment StartX=-55.5212 StartY=-44.982 StartZ=0 EndX=-54.7204 EndY=-44.982 EndZ=0
    g298: LineSegment StartX=-54.7204 StartY=-44.982 StartZ=0 EndX=-54.7204 EndY=-50.782 EndZ=0
    g299: LineSegment StartX=-54.7204 StartY=-50.782 StartZ=0 EndX=-55.5212 EndY=-50.782 EndZ=0
    g300: LineSegment StartX=-55.5212 StartY=-50.782 StartZ=0 EndX=-55.5212 EndY=-53.8826 EndZ=0
    g301: LineSegment StartX=-55.5212 StartY=-53.8826 StartZ=0 EndX=-54.7204 EndY=-53.8826 EndZ=0
    g302: LineSegment StartX=-54.7204 StartY=-53.8826 StartZ=0 EndX=-54.7204 EndY=-54.8816 EndZ=0
    g303: LineSegment StartX=-54.7204 StartY=-54.8816 StartZ=0 EndX=-40.7211 EndY=-54.8816 EndZ=0
    g304: LineSegment StartX=-59.7711 StartY=-54.8816 StartZ=0 EndX=-59.7711 EndY=-53.8826 EndZ=0
    g305: LineSegment StartX=-59.7711 StartY=-53.8826 StartZ=0 EndX=-58.9703 EndY=-53.8826 EndZ=0
    g306: LineSegment StartX=-58.9703 StartY=-53.8826 StartZ=0 EndX=-58.9703 EndY=-50.782 EndZ=0
    g307: LineSegment StartX=-58.9703 StartY=-50.782 StartZ=0 EndX=-59.7711 EndY=-50.782 EndZ=0
    g308: LineSegment StartX=-59.7711 StartY=-50.782 StartZ=0 EndX=-59.7711 EndY=-44.982 EndZ=0
    g309: LineSegment StartX=-59.7711 StartY=-44.982 StartZ=0 EndX=-58.9703 EndY=-44.982 EndZ=0
    g310: LineSegment StartX=-58.9703 StartY=-44.982 StartZ=0 EndX=-58.9703 EndY=-41.8828 EndZ=0
    g311: LineSegment StartX=-58.9703 StartY=-41.8828 StartZ=0 EndX=-59.7711 EndY=-41.8828 EndZ=0
    g312: LineSegment StartX=-59.7711 StartY=-41.8828 StartZ=0 EndX=-59.7711 EndY=-40.8824 EndZ=0
    g313: LineSegment StartX=-59.7711 StartY=-40.8824 StartZ=0 EndX=-73.7704 EndY=-40.8824 EndZ=0
    g314: LineSegment StartX=-73.7704 StartY=-40.8824 StartZ=0 EndX=-73.7704 EndY=-41.8828 EndZ=0
    g315: LineSegment StartX=-73.7704 StartY=-41.8828 StartZ=0 EndX=-74.5712 EndY=-41.8828 EndZ=0
    g316: LineSegment StartX=-74.5712 StartY=-41.8828 StartZ=0 EndX=-74.5712 EndY=-44.982 EndZ=0
    g317: LineSegment StartX=-74.5712 StartY=-44.982 StartZ=0 EndX=-73.7704 EndY=-44.982 EndZ=0
    g318: LineSegment StartX=-73.7704 StartY=-44.982 StartZ=0 EndX=-73.7704 EndY=-50.782 EndZ=0
    g319: LineSegment StartX=-73.7704 StartY=-50.782 StartZ=0 EndX=-74.5712 EndY=-50.782 EndZ=0
    g320: LineSegment StartX=-74.5712 StartY=-50.782 StartZ=0 EndX=-74.5712 EndY=-53.8826 EndZ=0
    g321: LineSegment StartX=-74.5712 StartY=-53.8826 StartZ=0 EndX=-73.7704 EndY=-53.8826 EndZ=0
    g322: LineSegment StartX=-73.7704 StartY=-53.8826 StartZ=0 EndX=-73.7704 EndY=-54.8816 EndZ=0
    g323: LineSegment StartX=-73.7704 StartY=-54.8816 StartZ=0 EndX=-59.7711 EndY=-54.8816 EndZ=0
    g324: LineSegment StartX=-78.8211 StartY=-54.8816 StartZ=0 EndX=-78.8211 EndY=-53.8826 EndZ=0
    g325: LineSegment StartX=-78.8211 StartY=-53.8826 StartZ=0 EndX=-78.0203 EndY=-53.8826 EndZ=0
    g326: LineSegment StartX=-78.0203 StartY=-53.8826 StartZ=0 EndX=-78.0203 EndY=-50.782 EndZ=0
    g327: LineSegment StartX=-78.0203 StartY=-50.782 StartZ=0 EndX=-78.8211 EndY=-50.782 EndZ=0
    g328: LineSegment StartX=-78.8211 StartY=-50.782 StartZ=0 EndX=-78.8211 EndY=-44.982 EndZ=0
    g329: LineSegment StartX=-78.8211 StartY=-44.982 StartZ=0 EndX=-78.0203 EndY=-44.982 EndZ=0
    g330: LineSegment StartX=-78.0203 StartY=-44.982 StartZ=0 EndX=-78.0203 EndY=-41.8828 EndZ=0
    g331: LineSegment StartX=-78.0203 StartY=-41.8828 StartZ=0 EndX=-78.8211 EndY=-41.8828 EndZ=0
    g332: LineSegment StartX=-78.8211 StartY=-41.8828 StartZ=0 EndX=-78.8211 EndY=-40.8824 EndZ=0
    g333: LineSegment StartX=-78.8211 StartY=-40.8824 StartZ=0 EndX=-92.8204 EndY=-40.8824 EndZ=0
    g334: LineSegment StartX=-92.8204 StartY=-40.8824 StartZ=0 EndX=-92.8204 EndY=-41.8828 EndZ=0
    g335: LineSegment StartX=-92.8204 StartY=-41.8828 StartZ=0 EndX=-93.6198 EndY=-41.8828 EndZ=0
    g336: LineSegment StartX=-93.6198 StartY=-41.8828 StartZ=0 EndX=-93.6198 EndY=-44.982 EndZ=0
    g337: LineSegment StartX=-93.6198 StartY=-44.982 StartZ=0 EndX=-92.8204 EndY=-44.982 EndZ=0
    g338: LineSegment StartX=-92.8204 StartY=-44.982 StartZ=0 EndX=-92.8204 EndY=-50.782 EndZ=0
    g339: LineSegment StartX=-92.8204 StartY=-50.782 StartZ=0 EndX=-93.6198 EndY=-50.782 EndZ=0
    g340: LineSegment StartX=-93.6198 StartY=-50.782 StartZ=0 EndX=-93.6198 EndY=-53.8826 EndZ=0
    g341: LineSegment StartX=-93.6198 StartY=-53.8826 StartZ=0 EndX=-92.8204 EndY=-53.8826 EndZ=0
    g342: LineSegment StartX=-92.8204 StartY=-53.8826 StartZ=0 EndX=-92.8204 EndY=-54.8816 EndZ=0
    g343: LineSegment StartX=-92.8204 StartY=-54.8816 StartZ=0 EndX=-78.8211 EndY=-54.8816 EndZ=0
    g344: LineSegment StartX=-21.671 StartY=-73.9316 StartZ=0 EndX=-21.671 EndY=-72.9326 EndZ=0
    g345: LineSegment StartX=-21.671 StartY=-72.9326 StartZ=0 EndX=-20.8704 EndY=-72.9326 EndZ=0
    g346: LineSegment StartX=-20.8704 StartY=-72.9326 StartZ=0 EndX=-20.8704 EndY=-69.832 EndZ=0
    g347: LineSegment StartX=-20.8704 StartY=-69.832 StartZ=0 EndX=-21.671 EndY=-69.832 EndZ=0
    g348: LineSegment StartX=-21.671 StartY=-69.832 StartZ=0 EndX=-21.671 EndY=-64.032 EndZ=0
    g349: LineSegment StartX=-21.671 StartY=-64.032 StartZ=0 EndX=-20.8704 EndY=-64.032 EndZ=0
    g350: LineSegment StartX=-20.8704 StartY=-64.032 StartZ=0 EndX=-20.8704 EndY=-60.9328 EndZ=0
    g351: LineSegment StartX=-20.8704 StartY=-60.9328 StartZ=0 EndX=-21.671 EndY=-60.9328 EndZ=0
    g352: LineSegment StartX=-21.671 StartY=-60.9328 StartZ=0 EndX=-21.671 EndY=-59.9324 EndZ=0
    g353: LineSegment StartX=-21.671 StartY=-59.9324 StartZ=0 EndX=-35.6704 EndY=-59.9324 EndZ=0
    g354: LineSegment StartX=-35.6704 StartY=-59.9324 StartZ=0 EndX=-35.6704 EndY=-60.9328 EndZ=0
    g355: LineSegment StartX=-35.6704 StartY=-60.9328 StartZ=0 EndX=-36.4712 EndY=-60.9328 EndZ=0
    g356: LineSegment StartX=-36.4712 StartY=-60.9328 StartZ=0 EndX=-36.4712 EndY=-64.032 EndZ=0
    g357: LineSegment StartX=-36.4712 StartY=-64.032 StartZ=0 EndX=-35.6704 EndY=-64.032 EndZ=0
    g358: LineSegment StartX=-35.6704 StartY=-64.032 StartZ=0 EndX=-35.6704 EndY=-69.832 EndZ=0
    g359: LineSegment StartX=-35.6704 StartY=-69.832 StartZ=0 EndX=-36.4712 EndY=-69.832 EndZ=0
    g360: LineSegment StartX=-36.4712 StartY=-69.832 StartZ=0 EndX=-36.4712 EndY=-72.9326 EndZ=0
    g361: LineSegment StartX=-36.4712 StartY=-72.9326 StartZ=0 EndX=-35.6704 EndY=-72.9326 EndZ=0
    g362: LineSegment StartX=-35.6704 StartY=-72.9326 StartZ=0 EndX=-35.6704 EndY=-73.9316 EndZ=0
    g363: LineSegment StartX=-35.6704 StartY=-73.9316 StartZ=0 EndX=-21.671 EndY=-73.9316 EndZ=0
    g364: LineSegment StartX=-40.7211 StartY=-73.9316 StartZ=0 EndX=-40.7211 EndY=-72.9326 EndZ=0
    g365: LineSegment StartX=-40.7211 StartY=-72.9326 StartZ=0 EndX=-39.9203 EndY=-72.9326 EndZ=0
    g366: LineSegment StartX=-39.9203 StartY=-72.9326 StartZ=0 EndX=-39.9203 EndY=-69.832 EndZ=0
    g367: LineSegment StartX=-39.9203 StartY=-69.832 StartZ=0 EndX=-40.7211 EndY=-69.832 EndZ=0
    g368: LineSegment StartX=-40.7211 StartY=-69.832 StartZ=0 EndX=-40.7211 EndY=-64.032 EndZ=0
    g369: LineSegment StartX=-40.7211 StartY=-64.032 StartZ=0 EndX=-39.9203 EndY=-64.032 EndZ=0
    g370: LineSegment StartX=-39.9203 StartY=-64.032 StartZ=0 EndX=-39.9203 EndY=-60.9328 EndZ=0
    g371: LineSegment StartX=-39.9203 StartY=-60.9328 StartZ=0 EndX=-40.7211 EndY=-60.9328 EndZ=0
    g372: LineSegment StartX=-40.7211 StartY=-60.9328 StartZ=0 EndX=-40.7211 EndY=-59.9324 EndZ=0
    g373: LineSegment StartX=-40.7211 StartY=-59.9324 StartZ=0 EndX=-54.7204 EndY=-59.9324 EndZ=0
    g374: LineSegment StartX=-54.7204 StartY=-59.9324 StartZ=0 EndX=-54.7204 EndY=-60.9328 EndZ=0
    g375: LineSegment StartX=-54.7204 StartY=-60.9328 StartZ=0 EndX=-55.5212 EndY=-60.9328 EndZ=0
    g376: LineSegment StartX=-55.5212 StartY=-60.9328 StartZ=0 EndX=-55.5212 EndY=-64.032 EndZ=0
    g377: LineSegment StartX=-55.5212 StartY=-64.032 StartZ=0 EndX=-54.7204 EndY=-64.032 EndZ=0
    g378: LineSegment StartX=-54.7204 StartY=-64.032 StartZ=0 EndX=-54.7204 EndY=-69.832 EndZ=0
    g379: LineSegment StartX=-54.7204 StartY=-69.832 StartZ=0 EndX=-55.5212 EndY=-69.832 EndZ=0
    g380: LineSegment StartX=-55.5212 StartY=-69.832 StartZ=0 EndX=-55.5212 EndY=-72.9326 EndZ=0
    g381: LineSegment StartX=-55.5212 StartY=-72.9326 StartZ=0 EndX=-54.7204 EndY=-72.9326 EndZ=0
    g382: LineSegment StartX=-54.7204 StartY=-72.9326 StartZ=0 EndX=-54.7204 EndY=-73.9316 EndZ=0
    g383: LineSegment StartX=-54.7204 StartY=-73.9316 StartZ=0 EndX=-40.7211 EndY=-73.9316 EndZ=0
    g384: LineSegment StartX=-59.7711 StartY=-73.9316 StartZ=0 EndX=-59.7711 EndY=-72.9326 EndZ=0
    g385: LineSegment StartX=-59.7711 StartY=-72.9326 StartZ=0 EndX=-58.9703 EndY=-72.9326 EndZ=0
    g386: LineSegment StartX=-58.9703 StartY=-72.9326 StartZ=0 EndX=-58.9703 EndY=-69.832 EndZ=0
    g387: LineSegment StartX=-58.9703 StartY=-69.832 StartZ=0 EndX=-59.7711 EndY=-69.832 EndZ=0
    g388: LineSegment StartX=-59.7711 StartY=-69.832 StartZ=0 EndX=-59.7711 EndY=-64.032 EndZ=0
    g389: LineSegment StartX=-59.7711 StartY=-64.032 StartZ=0 EndX=-58.9703 EndY=-64.032 EndZ=0
    g390: LineSegment StartX=-58.9703 StartY=-64.032 StartZ=0 EndX=-58.9703 EndY=-60.9328 EndZ=0
    g391: LineSegment StartX=-58.9703 StartY=-60.9328 StartZ=0 EndX=-59.7711 EndY=-60.9328 EndZ=0
    g392: LineSegment StartX=-59.7711 StartY=-60.9328 StartZ=0 EndX=-59.7711 EndY=-59.9324 EndZ=0
    g393: LineSegment StartX=-59.7711 StartY=-59.9324 StartZ=0 EndX=-73.7704 EndY=-59.9324 EndZ=0
    g394: LineSegment StartX=-73.7704 StartY=-59.9324 StartZ=0 EndX=-73.7704 EndY=-60.9328 EndZ=0
    g395: LineSegment StartX=-73.7704 StartY=-60.9328 StartZ=0 EndX=-74.5712 EndY=-60.9328 EndZ=0
    g396: LineSegment StartX=-74.5712 StartY=-60.9328 StartZ=0 EndX=-74.5712 EndY=-64.032 EndZ=0
    g397: LineSegment StartX=-74.5712 StartY=-64.032 StartZ=0 EndX=-73.7704 EndY=-64.032 EndZ=0
    g398: LineSegment StartX=-73.7704 StartY=-64.032 StartZ=0 EndX=-73.7704 EndY=-69.832 EndZ=0
    g399: LineSegment StartX=-73.7704 StartY=-69.832 StartZ=0 EndX=-74.5712 EndY=-69.832 EndZ=0
    ... +24 more geometry lines
FEATURE [PartDesign::Pad] Pad
  Direction = (0,0,1)
  Length = 1
  Length2 = 10
  Placement = pos=(0,0,0) rot=(0,0,1;3.14159rad)
  Profile = -> Sketch
  ReferenceAxis = -> Sketch [N_Axis]
  Type = 0
FEATURE [Sketcher::SketchObject] Sketch001
  ExternalGeometry = -> [Pad]
  FullyConstrained = true
  MapMode = 5
  Placement = pos=(0,0,1) rot=(0,0,1;3.14159rad)
  Support = -> [Pad]
  sketch-geometry (4):
    g0: LineSegment StartX=-0.0950846 StartY=-76.4575 StartZ=0 EndX=-18.671 EndY=-76.4575 EndZ=0
    g1: LineSegment StartX=-18.671 StartY=-76.4575 StartZ=0 EndX=-18.671 EndY=-19.7817 EndZ=0
    g2: LineSegment StartX=-18.671 StartY=-19.7817 StartZ=0 EndX=-0.0950846 EndY=-19.7817 EndZ=0
    g3: LineSegment StartX=-0.0950846 StartY=-19.7817 StartZ=0 EndX=-0.0950846 EndY=-76.4575 EndZ=0
  constraints (12):
    c: Coincident(g0,g1)
    c: Coincident(g1,g2)
    c: Coincident(g2,g3)
    c: Coincident(g3,g0)
    c: Horizontal(g0)
    c: Horizontal(g2)
    c: Vertical(g1)
    c: Vertical(g3)
    c: Horizontal(g0,g-3)
    c: Vertical(g-4,g0)
    c: DistanceX(g-7,g1) = 3
    c: DistanceY(g1,g-5) = 3
FEATURE [PartDesign::Pocket] Pocket
  BaseFeature = -> Pad
  Direction = (0,0,-1)
  Length = 5
  Length2 = 5
  Placement = pos=(0,0,0) rot=(0,0,1;3.14159rad)
  Profile = -> Sketch001
  ReferenceAxis = -> Sketch001 [N_Axis]
  Type = 1
FEATURE [PartDesign::Fillet] Fillet
  Base = -> Pocket [Edge878,Edge817,Edge7]
  BaseFeature = -> Pocket
  Placement = pos=(0,0,0) rot=(0,0,1;3.14159rad)
  Radius = 2
  SupportTransform = false
  UseAllEdges = false
FEATURE [PartDesign::Body] Body
  Group = -> [Sketch,Pad,Sketch001,Pocket,Fillet]
  Origin = -> Origin
  Tip = -> Fillet
